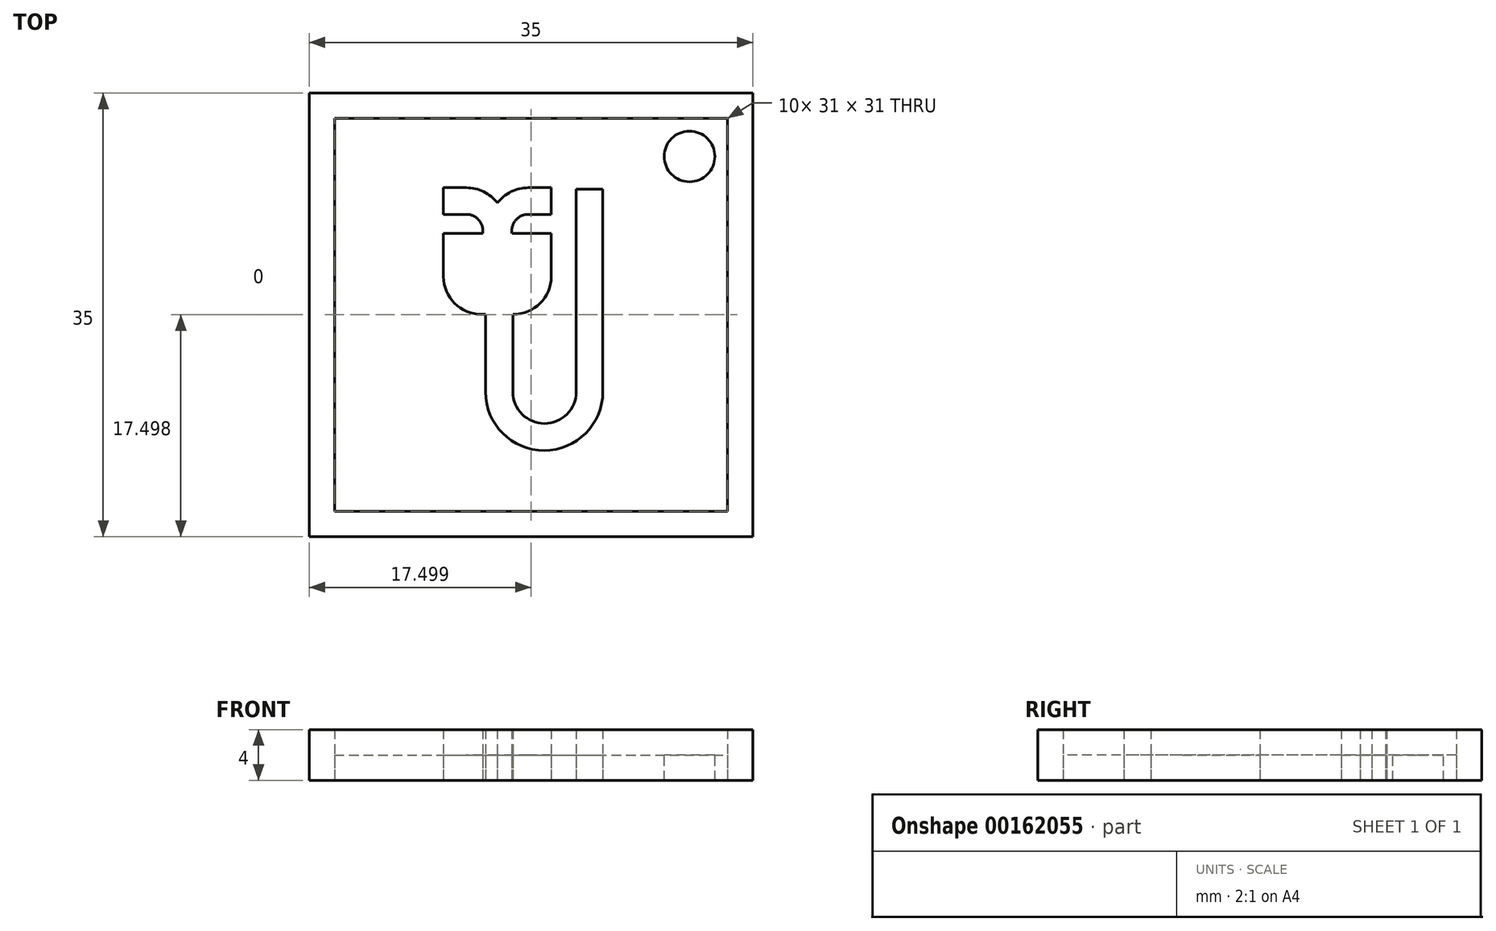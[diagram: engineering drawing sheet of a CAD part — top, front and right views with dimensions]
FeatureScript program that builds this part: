
annotation { "Feature Type Name" : "Feature", "Feature Type Description" : "" }
export const myFeature = defineFeature(function(context is Context, id is Id, definition is map)
    precondition{}
    {
        {
            var Q0;
            Q0=qCreatedBy(makeId("Top.planeOp"),FACE);
            var sketch = newSketch(context, id + "F0", { "sketchPlane" : qUnion([Q0])});
            skLineSegment(sketch, "E0.bottom", {"start": v(-12.05, 16.49) * mm, "end": v(22.95, 16.49) * mm});
            skLineSegment(sketch, "E0.top", {"start": v(-12.05, -18.51) * mm, "end": v(22.95, -18.51) * mm});
            skLineSegment(sketch, "E0.left", {"start": v(-12.05, 16.49) * mm, "end": v(-12.05, -18.51) * mm});
            skLineSegment(sketch, "E1.0", {"start": v(-10.05, 14.49) * mm, "end": v(20.95, 14.49) * mm});
            skLineSegment(sketch, "E1.1", {"start": v(-10.05, 14.49) * mm, "end": v(-10.05, -16.51) * mm});
            skLineSegment(sketch, "E1.2", {"start": v(-10.05, -16.51) * mm, "end": v(20.95, -16.51) * mm});
            skLineSegment(sketch, "E1.3", {"start": v(20.95, 14.49) * mm, "end": v(20.95, -16.51) * mm});
            skLineSegment(sketch, "E2.bottom", {"start": v(9, 8.9) * mm, "end": v(11.1, 8.9) * mm});
            skLineSegment(sketch, "E2.top", {"start": v(9, -7.1) * mm, "end": v(11.1, -7.1) * mm});
            skLineSegment(sketch, "E2.left", {"start": v(9, 8.9) * mm, "end": v(9, -7.1) * mm});
            skLineSegment(sketch, "E2.right", {"start": v(11.1, 8.9) * mm, "end": v(11.1, -7.1) * mm});
            skArc(sketch, "E3", {"start": v(1.86, -7.1) * mm, "mid": v(6.48, -11.72) * mm, "end": v(11.1, -7.1) * mm});
            skArc(sketch, "E4", {"start": v(4.02, -7.1) * mm, "mid": v(6.51, -9.59) * mm, "end": v(9, -7.1) * mm});
            skLineSegment(sketch, "E5.bottom", {"start": v(1.86, -7.1) * mm, "end": v(4.02, -7.1) * mm});
            skLineSegment(sketch, "E5.top", {"start": v(1.86, -0.98) * mm, "end": v(4.02, -0.98) * mm});
            skLineSegment(sketch, "E5.left", {"start": v(1.86, -7.1) * mm, "end": v(1.86, -0.98) * mm});
            skLineSegment(sketch, "E5.right", {"start": v(4.02, -7.1) * mm, "end": v(4.02, -0.98) * mm});
            skLineSegment(sketch, "E6.bottom", {"start": v(-1.46, 5.42) * mm, "end": v(7.04, 5.42) * mm});
            skLineSegment(sketch, "E6.top", {"start": v(1.54, -0.98) * mm, "end": v(4.04, -0.98) * mm});
            skLineSegment(sketch, "E6.left", {"start": v(-1.46, 5.42) * mm, "end": v(-1.46, 2.02) * mm});
            skLineSegment(sketch, "E6.right", {"start": v(7.04, 5.42) * mm, "end": v(7.04, 2.02) * mm});
            skPoint(sketch, "E7.visualSharp", {"position": v(-1.46, -0.98) * mm});
            skArc(sketch, "E7.filletArc", {"start": v(-1.46, 2.02) * mm, "mid": v(-0.58, -0.1) * mm, "end": v(1.54, -0.98) * mm});
            skPoint(sketch, "E8.visualSharp", {"position": v(7.04, -0.98) * mm});
            skArc(sketch, "E8.filletArc", {"start": v(4.04, -0.98) * mm, "mid": v(6.16, -0.1) * mm, "end": v(7.04, 2.02) * mm});
            skLineSegment(sketch, "E9", {"start": v(2.8, 5.42) * mm, "end": v(2.8, 7.82) * mm});
            skLineSegment(sketch, "E10", {"start": v(7.04, 6.92) * mm, "end": v(7.04, 9.02) * mm});
            skLineSegment(sketch, "E11", {"start": v(7.04, 9.02) * mm, "end": v(5.24, 9.02) * mm});
            skArc(sketch, "E12", {"start": v(5.24, 9.02) * mm, "mid": v(3.88, 8.7) * mm, "end": v(2.8, 7.82) * mm});
            skLineSegment(sketch, "E13", {"start": v(7.04, 6.92) * mm, "end": v(5.24, 6.92) * mm});
            skArc(sketch, "E14", {"start": v(5.24, 6.92) * mm, "mid": v(4.25, 6.47) * mm, "end": v(3.94, 5.42) * mm});
            skArc(sketch, "E15.MirrorCS", {"start": v(0.34, 6.92) * mm, "mid": v(1.33, 6.47) * mm, "end": v(1.64, 5.42) * mm});
            skLineSegment(sketch, "E16.MirrorCS", {"start": v(-1.46, 6.92) * mm, "end": v(0.34, 6.92) * mm});
            skLineSegment(sketch, "E17.MirrorCS", {"start": v(-1.46, 6.92) * mm, "end": v(-1.46, 9.02) * mm});
            skLineSegment(sketch, "E18.MirrorCS", {"start": v(-1.46, 9.02) * mm, "end": v(0.34, 9.02) * mm});
            skArc(sketch, "E19.MirrorCS", {"start": v(0.34, 9.02) * mm, "mid": v(1.7, 8.7) * mm, "end": v(2.8, 7.82) * mm});
            skLineSegment(sketch, "E20", {"start": v(22.95, 16.49) * mm, "end": v(22.95, -18.51) * mm});
            skSolve(sketch);
        }
        {
            var Q0;
            Q0 = qSketchRegion(id + "F0", true);
            var Q1;
            {var subQ0=sQuery(id+"F0.wireOp",EDGE,"E6.left");Q1=makeQuery(id+"F0.imprint","IMPRINT",FACE,{"disambiguationData":[TD([[makeQuery(id+"F0.imprint","IMPRINT",EDGE,{"derivedFrom":subQ0}),1.0]])]});}
            var Q2;
            {var subQ0=sQuery(id+"F0.wireOp",EDGE,"E9");Q2=makeQuery(id+"F0.imprint","IMPRINT",FACE,{"disambiguationData":[TD([[makeQuery(id+"F0.imprint","IMPRINT",EDGE,{"derivedFrom":subQ0}),1.0]])]});}
            var Q3;
            {var subQ1=sQuery(id+"F0.wireOp",EDGE,"E9");Q3=makeQuery(id+"F0.imprint","IMPRINT",FACE,{"disambiguationData":[TD([[makeQuery(id+"F0.imprint","IMPRINT",EDGE,{"derivedFrom":subQ1}),-1.0]])]});}
            var Q4;
            Q4=makeQuery(id+"F0.imprint","IMPRINT",FACE,{"disambiguationData":[TD([[makeQuery(id+"F0.imprint","IMPRINT",EDGE,{"derivedFrom":sQuery(id+"F0.wireOp",EDGE,"E2.bottom")}),-1.0]])]});
            var Q5;
            Q5=makeQuery(id+"F0.imprint","IMPRINT",FACE,{"disambiguationData":[TD([[makeQuery(id+"F0.imprint","IMPRINT",EDGE,{"derivedFrom":sQuery(id+"F0.wireOp",EDGE,"E2.top")}),-1.0]])]});
            var Q6;
            Q6=makeQuery(id+"F0.imprint","IMPRINT",FACE,{"disambiguationData":[TD([[makeQuery(id+"F0.imprint","IMPRINT",EDGE,{"derivedFrom":sQuery(id+"F0.wireOp",EDGE,"E5.bottom")}),1.0]])]});
            extrude(context, id + "F1", {"entities" : qUnion([Q0, Q1, Q2, Q3, Q4, Q5, Q6]), "depth" : 4 * mm});
        }
        {
            var Q0;
            Q0=makeQuery(id+"F0.imprint","IMPRINT",FACE,{"disambiguationData":[TD([[makeQuery(id+"F0.imprint","IMPRINT",EDGE,{"derivedFrom":sQuery(id+"F0.wireOp",EDGE,"E1.0")}),-1.0]])]});
            extrude(context, id + "F2", {"entities" : qUnion([Q0]), "depth" : 2 * mm});
        }
        {
            var Q0;
            Q0=makeQuery(id+"F2.opExtrude","CAP_FACE",FACE,{"disambiguationData":[OSD([sQuery(id+"F0.wireOp",EDGE,"E1.0"),sQuery(id+"F0.wireOp",EDGE,"E1.1"),sQuery(id+"F0.wireOp",EDGE,"E1.2"),sQuery(id+"F0.wireOp",EDGE,"E1.3"),sQuery(id+"F0.wireOp",EDGE,"E2.bottom"),sQuery(id+"F0.wireOp",EDGE,"E2.left"),sQuery(id+"F0.wireOp",EDGE,"E2.right"),sQuery(id+"F0.wireOp",EDGE,"E3"),sQuery(id+"F0.wireOp",EDGE,"E4"),sQuery(id+"F0.wireOp",EDGE,"E5.left"),sQuery(id+"F0.wireOp",EDGE,"E5.right"),sQuery(id+"F0.wireOp",EDGE,"E6.bottom"),sQuery(id+"F0.wireOp",EDGE,"E6.top"),sQuery(id+"F0.wireOp",EDGE,"E6.left"),sQuery(id+"F0.wireOp",EDGE,"E6.right"),sQuery(id+"F0.wireOp",EDGE,"E7.filletArc"),sQuery(id+"F0.wireOp",EDGE,"E8.filletArc"),sQuery(id+"F0.wireOp",EDGE,"E10"),sQuery(id+"F0.wireOp",EDGE,"E11"),sQuery(id+"F0.wireOp",EDGE,"E12"),sQuery(id+"F0.wireOp",EDGE,"E13"),sQuery(id+"F0.wireOp",EDGE,"E14"),sQuery(id+"F0.wireOp",EDGE,"E15.MirrorCS"),sQuery(id+"F0.wireOp",EDGE,"E16.MirrorCS"),sQuery(id+"F0.wireOp",EDGE,"E17.MirrorCS"),sQuery(id+"F0.wireOp",EDGE,"E18.MirrorCS"),sQuery(id+"F0.wireOp",EDGE,"E19.MirrorCS")])],"isStart":false});
            var sketch = newSketch(context, id + "F3", { "sketchPlane" : qUnion([Q0])});
            skPoint(sketch, "E21", {"position": v(17.95, 11.49) * mm});
            skSolve(sketch);
        }
        {
            var Q0;
            Q0=sQuery(id+"F3.wireOp",VERTEX,"E21");
            var Q1;
            Q1=makeQuery(id+"F2.opExtrude","SWEPT_BODY",BODY,{"disambiguationData":[OSD([sQuery(id+"F0.wireOp",EDGE,"E1.0"),sQuery(id+"F0.wireOp",EDGE,"E1.1"),sQuery(id+"F0.wireOp",EDGE,"E1.2"),sQuery(id+"F0.wireOp",EDGE,"E1.3"),sQuery(id+"F0.wireOp",EDGE,"E2.bottom"),sQuery(id+"F0.wireOp",EDGE,"E2.left"),sQuery(id+"F0.wireOp",EDGE,"E2.right"),sQuery(id+"F0.wireOp",EDGE,"E3"),sQuery(id+"F0.wireOp",EDGE,"E4"),sQuery(id+"F0.wireOp",EDGE,"E5.left"),sQuery(id+"F0.wireOp",EDGE,"E5.right"),sQuery(id+"F0.wireOp",EDGE,"E6.bottom"),sQuery(id+"F0.wireOp",EDGE,"E6.top"),sQuery(id+"F0.wireOp",EDGE,"E6.left"),sQuery(id+"F0.wireOp",EDGE,"E6.right"),sQuery(id+"F0.wireOp",EDGE,"E7.filletArc"),sQuery(id+"F0.wireOp",EDGE,"E8.filletArc"),sQuery(id+"F0.wireOp",EDGE,"E10"),sQuery(id+"F0.wireOp",EDGE,"E11"),sQuery(id+"F0.wireOp",EDGE,"E12"),sQuery(id+"F0.wireOp",EDGE,"E13"),sQuery(id+"F0.wireOp",EDGE,"E14"),sQuery(id+"F0.wireOp",EDGE,"E15.MirrorCS"),sQuery(id+"F0.wireOp",EDGE,"E16.MirrorCS"),sQuery(id+"F0.wireOp",EDGE,"E17.MirrorCS"),sQuery(id+"F0.wireOp",EDGE,"E18.MirrorCS"),sQuery(id+"F0.wireOp",EDGE,"E19.MirrorCS")])]});
            hole(context, id + "F4", {"style" : HoleStyle.SIMPLE, "endStyle" : HoleEndStyle.THROUGH, "holeDiameter" : 4 * mm, "locations" : qUnion([Q0]), "scope" : qUnion([Q1]), "isTappedThrough" : true});
        }
    });
